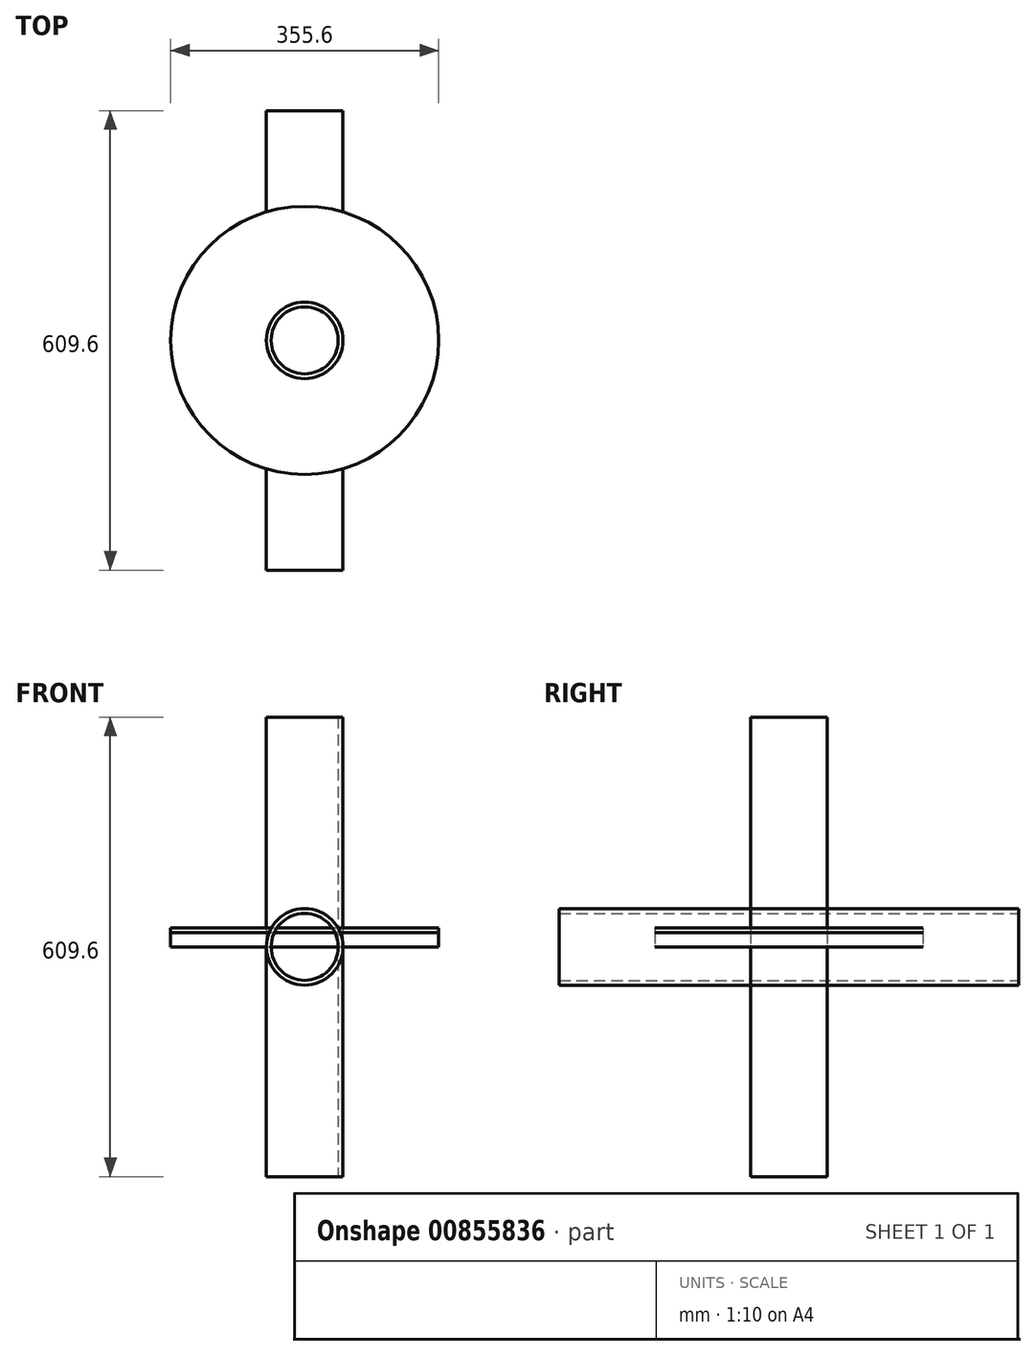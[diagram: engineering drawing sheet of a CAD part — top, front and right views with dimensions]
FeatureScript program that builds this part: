
annotation { "Feature Type Name" : "Feature", "Feature Type Description" : "" }
export const myFeature = defineFeature(function(context is Context, id is Id, definition is map)
    precondition{}
    {
        {
            var Q0;
            Q0=qCreatedBy(makeId("Front.planeOp"),FACE);
            var sketch = newSketch(context, id + "F0", { "sketchPlane" : qUnion([Q0])});
            skCircle(sketch, "E0", {"center": v(0, 0) * mm, "radius": 50.8 * mm});
            skCircle(sketch, "E1", {"center": v(0, 0) * mm, "radius": 44.45 * mm});
            skSolve(sketch);
        }
        {
            var Q0;
            Q0 = qSketchRegion(id + "F0", true);
            extrude(context, id + "F1", {"entities" : qUnion([Q0]), "endBound" : BoundingType.SYMMETRIC, "depth" : 609.6 * mm, "offsetDistance" : 25.4 * mm});
        }
        {
            var Q0;
            Q0=qCreatedBy(makeId("Top.planeOp"),FACE);
            var sketch = newSketch(context, id + "F2", { "sketchPlane" : qUnion([Q0])});
            skCircle(sketch, "E2", {"center": v(0, 0) * mm, "radius": 50.8 * mm});
            skCircle(sketch, "E3", {"center": v(0, 0) * mm, "radius": 44.45 * mm});
            skSolve(sketch);
        }
        {
            var Q0;
            Q0 = qSketchRegion(id + "F2", true);
            extrude(context, id + "F3", {"entities" : qUnion([Q0]), "endBound" : BoundingType.SYMMETRIC, "depth" : 609.6 * mm, "offsetDistance" : 25.4 * mm});
        }
        {
            var Q0;
            Q0=qCreatedBy(makeId("Top.planeOp"),FACE);
            var sketch = newSketch(context, id + "F4", { "sketchPlane" : qUnion([Q0])});
            skCircle(sketch, "E4", {"center": v(0, 0) * mm, "radius": 177.8 * mm});
            skCircle(sketch, "E5", {"center": v(0, 0) * mm, "radius": 50.8 * mm});
            skSolve(sketch);
        }
        {
            var Q0;
            Q0 = qSketchRegion(id + "F4", true);
            extrude(context, id + "F5", {"entities" : qUnion([Q0]), "depth" : 19.05 * mm, "offsetDistance" : 25.4 * mm});
        }
        {
            var Q0;
            Q0=qCreatedBy(makeId("Top.planeOp"),FACE);
            var sketch = newSketch(context, id + "F6", { "sketchPlane" : qUnion([Q0])});
            skCircle(sketch, "E6", {"center": v(0, 0) * mm, "radius": 177.8 * mm});
            skCircle(sketch, "E7", {"center": v(0, 0) * mm, "radius": 50.8 * mm});
            skSolve(sketch);
        }
        {
            var Q0;
            Q0 = qSketchRegion(id + "F6", true);
            extrude(context, id + "F7", {"entities" : qUnion([Q0]), "depth" : 25.4 * mm, "offsetDistance" : 25.4 * mm});
        }
    });
